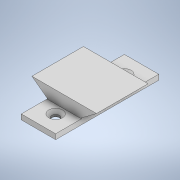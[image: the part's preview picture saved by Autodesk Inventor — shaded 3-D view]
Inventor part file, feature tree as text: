
AUTODESK INVENTOR PART (.ipt)
format: ipt  version: 2022.3 (Build 263350000, 350)  size: 130,048 bytes
history: native  units: mm
features: thicken_offset x3, sketch x3, extrude x2, hole x1
ambient origin geometry x8: Origin, YZ Plane, XZ Plane, XY Plane, X Axis, Y Axis, Z Axis, Center Point
bodies: Solid1 (feature_tree)
feature tree (9):
  extrude  "Extrusion1"  Depth=30.0mm
  hole  "Hole1"  [1 undecoded]
  extrude  "Extrusion2"  Depth=7.5mm
  thicken_offset  "Thicken1"
  thicken_offset  "Thicken2"
  thicken_offset  "Thicken3"
  sketch  "Sketch1"  dims[d0=10.0mm d1=30.0mm]
  sketch  "Sketch2"  dims[d2=1.5mm d3=0.0mm d4=10.0mm]
  sketch  "Sketch3"  dims[d5=20.0mm d6=2.2mm d7=6.0mm d8=4.0mm d9=2.0mm d10=90.0deg d11=0.9mm d12=0.0mm d13=20.0mm d14=7.5mm d15=7.5mm d16=7.5mm d17=0.0mm d18=0.0mm d19=0.2mm d20=0.2mm d21=0.2mm d22=0.2mm d23=0.2mm d24=0.2mm]
note: 1 required parameter value undecoded (feature->parameter linkage not recoverable at this tier; creation-order binding heuristic only, values carry confidence <= 0.55)
